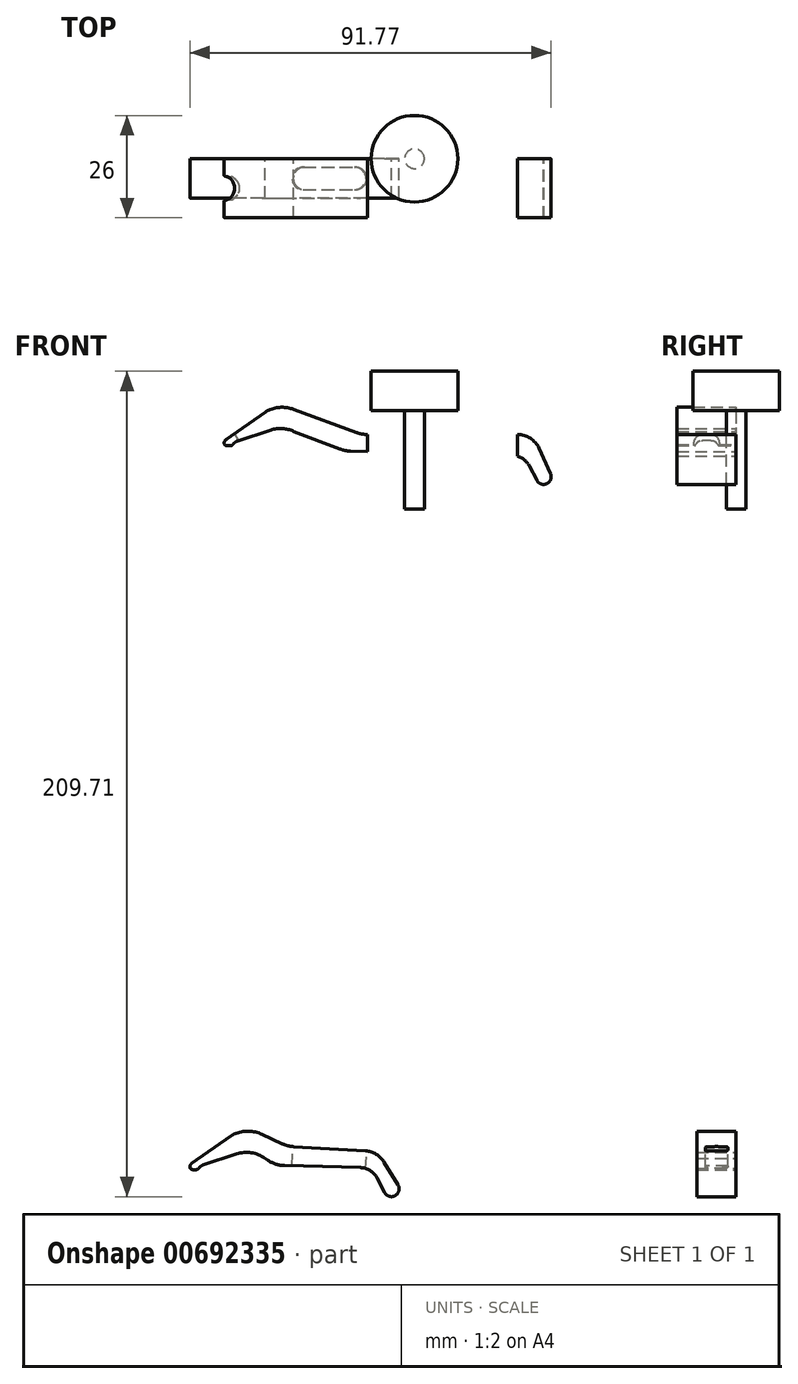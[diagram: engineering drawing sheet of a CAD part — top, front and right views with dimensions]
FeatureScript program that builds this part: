
annotation { "Feature Type Name" : "Feature", "Feature Type Description" : "" }
export const myFeature = defineFeature(function(context is Context, id is Id, definition is map)
    precondition{}
    {
        {
            var Q0;
            Q0=qCreatedBy(makeId("Front.planeOp"),FACE);
            var sketch = newSketch(context, id + "F0", { "sketchPlane" : qUnion([Q0])});
            skLineSegment(sketch, "E0.bottom", {"start": v(-71.92, 0) * mm, "end": v(4.68, 0) * mm});
            skLineSegment(sketch, "E0.top", {"start": v(-71.92, 5) * mm, "end": v(4.68, 5) * mm});
            skLineSegment(sketch, "E0.left", {"start": v(-71.92, 0) * mm, "end": v(-71.92, 5) * mm});
            skLineSegment(sketch, "E0.right", {"start": v(4.68, 0) * mm, "end": v(4.68, 5) * mm});
            skLineSegment(sketch, "E1.bottom", {"start": v(-61.54, 15) * mm, "end": v(0, 15) * mm});
            skLineSegment(sketch, "E1.top", {"start": v(-61.54, 5) * mm, "end": v(0, 5) * mm});
            skLineSegment(sketch, "E1.left", {"start": v(-61.54, 15) * mm, "end": v(-61.54, 5) * mm});
            skLineSegment(sketch, "E1.right", {"start": v(0, 15) * mm, "end": v(0, 5) * mm});
            skLineSegment(sketch, "E2", {"start": v(-10, 41.21) * mm, "end": v(-10, -87.98) * mm, "construction": true});
            skLineSegment(sketch, "E3", {"start": v(69.92, 0) * mm, "end": v(70.03, 0) * mm});
            skLineSegment(sketch, "E4", {"start": v(71.74, 2.83) * mm, "end": v(68.83, 9.2) * mm});
            skLineSegment(sketch, "E5", {"start": v(63.37, 12.7) * mm, "end": v(25.24, 12.7) * mm});
            skPoint(sketch, "E6.visualSharp", {"position": v(50, 0) * mm});
            skPoint(sketch, "E7.visualSharp", {"position": v(73.03, 0) * mm});
            skArc(sketch, "E7.filletArc", {"start": v(69.92, 0) * mm, "mid": v(71.6, 0.92) * mm, "end": v(71.74, 2.83) * mm});
            skLineSegment(sketch, "E8", {"start": v(37.19, 28.77) * mm, "end": v(37.19, -6.23) * mm});
            skLineSegment(sketch, "E9", {"start": v(37.19, -6.23) * mm, "end": v(39.69, -6.23) * mm});
            skLineSegment(sketch, "E10", {"start": v(39.69, -6.23) * mm, "end": v(39.69, 18.77) * mm});
            skLineSegment(sketch, "E11", {"start": v(39.69, 18.77) * mm, "end": v(48.19, 18.77) * mm});
            skLineSegment(sketch, "E12", {"start": v(48.19, 18.77) * mm, "end": v(48.19, 28.77) * mm});
            skLineSegment(sketch, "E13", {"start": v(48.19, 28.77) * mm, "end": v(37.19, 28.77) * mm});
            skLineSegment(sketch, "E14", {"start": v(6.53, 19.1) * mm, "end": v(22.47, 13.2) * mm});
            skArc(sketch, "E15.filletArc", {"start": v(6.53, 19.1) * mm, "mid": v(3.34, 19.62) * mm, "end": v(0.17, 18.91) * mm});
            skPoint(sketch, "E16.visualSharp", {"position": v(23.8, 12.7) * mm});
            skArc(sketch, "E16.filletArc", {"start": v(22.47, 13.2) * mm, "mid": v(23.83, 12.83) * mm, "end": v(25.24, 12.7) * mm});
            skLineSegment(sketch, "E17", {"start": v(68.26, 1.07) * mm, "end": v(66.35, 4.72) * mm});
            skLineSegment(sketch, "E18", {"start": v(-0.7, 18.42) * mm, "end": v(-10.73, 11.4) * mm});
            skLineSegment(sketch, "E19", {"start": v(20.96, 8.48) * mm, "end": v(62.06, 7.4) * mm});
            skLineSegment(sketch, "E20", {"start": v(6.52, 13.5) * mm, "end": v(18.33, 9) * mm});
            skLineSegment(sketch, "E21", {"start": v(0.7, 13.82) * mm, "end": v(-7.82, 11.02) * mm});
            skPoint(sketch, "E22.visualSharp", {"position": v(-0.38, 18.65) * mm});
            skArc(sketch, "E22.filletArc", {"start": v(0.17, 18.91) * mm, "mid": v(-0.27, 18.69) * mm, "end": v(-0.7, 18.42) * mm});
            skArc(sketch, "E23", {"start": v(0.7, 13.82) * mm, "mid": v(3.64, 14.21) * mm, "end": v(6.52, 13.5) * mm});
            skLineSegment(sketch, "E24", {"start": v(-11.16, 10.27) * mm, "end": v(-10.98, 10) * mm});
            skLineSegment(sketch, "E25", {"start": v(-10.35, 9.84) * mm, "end": v(-9.65, 9.84) * mm});
            skLineSegment(sketch, "E26", {"start": v(-8.84, 10.27) * mm, "end": v(-8.83, 10.27) * mm});
            skPoint(sketch, "E27.visualSharp", {"position": v(-10.87, 9.84) * mm});
            skArc(sketch, "E27.filletArc", {"start": v(-11.16, 10.27) * mm, "mid": v(-10.8, 9.95) * mm, "end": v(-10.35, 9.84) * mm});
            skPoint(sketch, "E28.visualSharp", {"position": v(-9.13, 9.84) * mm});
            skArc(sketch, "E28.filletArc", {"start": v(-9.65, 9.84) * mm, "mid": v(-9.2, 9.95) * mm, "end": v(-8.84, 10.27) * mm});
            skPoint(sketch, "E29.visualSharp", {"position": v(-11.55, 10.82) * mm});
            skArc(sketch, "E29.filletArc", {"start": v(-10.73, 11.4) * mm, "mid": v(-11.14, 10.75) * mm, "end": v(-10.98, 10) * mm});
            skPoint(sketch, "E30.visualSharp", {"position": v(-8.45, 10.82) * mm});
            skArc(sketch, "E30.filletArc", {"start": v(-7.82, 11.02) * mm, "mid": v(-8.38, 10.73) * mm, "end": v(-8.83, 10.27) * mm});
            skPoint(sketch, "E31.visualSharp", {"position": v(19.6, 8.52) * mm});
            skArc(sketch, "E31.filletArc", {"start": v(18.33, 9) * mm, "mid": v(19.62, 8.63) * mm, "end": v(20.96, 8.48) * mm});
            skPoint(sketch, "E32.visualSharp", {"position": v(67.23, 12.7) * mm});
            skArc(sketch, "E32.filletArc", {"start": v(68.83, 9.2) * mm, "mid": v(66.61, 11.76) * mm, "end": v(63.37, 12.7) * mm});
            skPoint(sketch, "E33.visualSharp", {"position": v(65, 7.32) * mm});
            skArc(sketch, "E33.filletArc", {"start": v(66.35, 4.72) * mm, "mid": v(64.57, 6.64) * mm, "end": v(62.06, 7.4) * mm});
            skPoint(sketch, "E34.visualSharp", {"position": v(68.82, 0) * mm});
            skArc(sketch, "E34.filletArc", {"start": v(68.26, 1.07) * mm, "mid": v(69, 0.29) * mm, "end": v(70.03, 0) * mm});
            skLineSegment(sketch, "E35", {"start": v(31.28, -180.94) * mm, "end": v(31.4, -180.94) * mm});
            skLineSegment(sketch, "E36", {"start": v(32.99, -177.9) * mm, "end": v(29.5, -172.18) * mm});
            skLineSegment(sketch, "E37", {"start": v(24.73, -169.32) * mm, "end": v(6.47, -168.23) * mm});
            skPoint(sketch, "E38.visualSharp", {"position": v(34.85, -180.94) * mm});
            skArc(sketch, "E38.filletArc", {"start": v(31.28, -180.94) * mm, "mid": v(33.02, -179.92) * mm, "end": v(32.99, -177.9) * mm});
            skLineSegment(sketch, "E39", {"start": v(-1.5, -165.11) * mm, "end": v(3.55, -167.48) * mm});
            skArc(sketch, "E40.filletArc", {"start": v(-1.5, -165.11) * mm, "mid": v(-5, -164.3) * mm, "end": v(-8.52, -165.01) * mm});
            skPoint(sketch, "E41.visualSharp", {"position": v(4.94, -168.14) * mm});
            skArc(sketch, "E41.filletArc", {"start": v(3.55, -167.48) * mm, "mid": v(4.98, -168) * mm, "end": v(6.47, -168.23) * mm});
            skLineSegment(sketch, "E42", {"start": v(29.62, -179.87) * mm, "end": v(27.71, -176.23) * mm});
            skLineSegment(sketch, "E43", {"start": v(-9.4, -165.5) * mm, "end": v(-19.43, -172.53) * mm});
            skLineSegment(sketch, "E44", {"start": v(4.16, -173.04) * mm, "end": v(23.42, -173.55) * mm});
            skLineSegment(sketch, "E45", {"start": v(-0.82, -171.21) * mm, "end": v(0.03, -171.76) * mm});
            skLineSegment(sketch, "E46", {"start": v(-8, -170.1) * mm, "end": v(-16.51, -172.9) * mm});
            skPoint(sketch, "E47.visualSharp", {"position": v(-9.07, -165.28) * mm});
            skArc(sketch, "E47.filletArc", {"start": v(-8.52, -165.01) * mm, "mid": v(-8.97, -165.24) * mm, "end": v(-9.4, -165.5) * mm});
            skArc(sketch, "E48", {"start": v(-8, -170.1) * mm, "mid": v(-4.28, -169.8) * mm, "end": v(-0.82, -171.21) * mm});
            skLineSegment(sketch, "E49", {"start": v(-19.86, -173.66) * mm, "end": v(-19.67, -173.93) * mm});
            skLineSegment(sketch, "E50", {"start": v(-19.04, -174.08) * mm, "end": v(-18.35, -174.08) * mm});
            skLineSegment(sketch, "E51", {"start": v(-17.53, -173.66) * mm, "end": v(-17.53, -173.65) * mm});
            skPoint(sketch, "E52.visualSharp", {"position": v(-19.56, -174.08) * mm});
            skArc(sketch, "E52.filletArc", {"start": v(-19.86, -173.66) * mm, "mid": v(-19.5, -173.97) * mm, "end": v(-19.04, -174.08) * mm});
            skPoint(sketch, "E53.visualSharp", {"position": v(-17.83, -174.08) * mm});
            skArc(sketch, "E53.filletArc", {"start": v(-18.35, -174.08) * mm, "mid": v(-17.89, -173.97) * mm, "end": v(-17.53, -173.66) * mm});
            skPoint(sketch, "E54.visualSharp", {"position": v(-20.25, -173.1) * mm});
            skArc(sketch, "E54.filletArc", {"start": v(-19.43, -172.53) * mm, "mid": v(-19.84, -173.18) * mm, "end": v(-19.67, -173.93) * mm});
            skPoint(sketch, "E55.visualSharp", {"position": v(-17.14, -173.1) * mm});
            skArc(sketch, "E55.filletArc", {"start": v(-16.51, -172.9) * mm, "mid": v(-17.08, -173.2) * mm, "end": v(-17.53, -173.65) * mm});
            skPoint(sketch, "E56.visualSharp", {"position": v(1.91, -172.98) * mm});
            skArc(sketch, "E56.filletArc", {"start": v(0.03, -171.76) * mm, "mid": v(2, -172.68) * mm, "end": v(4.16, -173.04) * mm});
            skPoint(sketch, "E57.visualSharp", {"position": v(27.86, -169.51) * mm});
            skArc(sketch, "E57.filletArc", {"start": v(29.5, -172.18) * mm, "mid": v(27.46, -170.17) * mm, "end": v(24.73, -169.32) * mm});
            skPoint(sketch, "E58.visualSharp", {"position": v(26.35, -173.63) * mm});
            skArc(sketch, "E58.filletArc", {"start": v(27.71, -176.23) * mm, "mid": v(25.93, -174.3) * mm, "end": v(23.42, -173.55) * mm});
            skPoint(sketch, "E59.visualSharp", {"position": v(30.18, -180.94) * mm});
            skArc(sketch, "E59.filletArc", {"start": v(29.62, -179.87) * mm, "mid": v(30.36, -180.65) * mm, "end": v(31.4, -180.94) * mm});
            skSolve(sketch);
        }
        {
            var Q0;
            Q0=makeQuery(id+"F0.imprint","IMPRINT",FACE,{"disambiguationData":[TD([[makeQuery(id+"F0.imprint","IMPRINT",EDGE,{"derivedFrom":sQuery(id+"F0.wireOp",EDGE,"chy2nytO-zmfl-5nmg-iIkC-2bCcduLToJEE")}),1.0]])]});
            var Q1;
            {var subQ0=sQuery(id+"F0.wireOp",EDGE,"E8");var subQ1=sQuery(id+"F0.wireOp",EDGE,"1yFlV4U2-wMyq-fvNE-aanu-wgkpqW72YXBd");var subQ2=makeQuery(id+"F0.imprint","INTERSECT",VERTEX,{"derivedFrom":[subQ1,subQ0]});Q1=makeQuery(id+"F0.imprint","IMPRINT",FACE,{"disambiguationData":[TD([[makeQuery(id+"F0.imprint","IMPRINT",EDGE,{"disambiguationData":[TD([[subQ2,-1.0]])],"derivedFrom":subQ1}),1.0]])]});}
            var Q2;
            Q2=makeQuery(id+"F0.imprint","IMPRINT",FACE,{"disambiguationData":[TD([[makeQuery(id+"F0.imprint","IMPRINT",EDGE,{"derivedFrom":sQuery(id+"F0.wireOp",EDGE,"6blI8IkM-XKw8-aW75-wXaW-XcNFNPNdMWHI")}),1.0]])]});
            var Q3;
            Q3=makeQuery(id+"F0.imprint","IMPRINT",FACE,{"disambiguationData":[TD([[makeQuery(id+"F0.imprint","IMPRINT",EDGE,{"derivedFrom":sQuery(id+"F0.wireOp",EDGE,"E3")}),1.0]])]});
            var Q4;
            Q4=makeQuery(id+"F0.imprint","IMPRINT",FACE,{"disambiguationData":[TD([[makeQuery(id+"F0.imprint","IMPRINT",EDGE,{"derivedFrom":sQuery(id+"F0.wireOp",EDGE,"654yBweP-M0h2-mpYu-GDyn-SHg2XxIWOSnG")}),1.0]])]});
            var Q5;
            Q5=makeQuery(id+"F0.imprint","IMPRINT",FACE,{"disambiguationData":[TD([[makeQuery(id+"F0.imprint","IMPRINT",EDGE,{"derivedFrom":sQuery(id+"F0.wireOp",EDGE,"E14")}),-1.0]])]});
            var Q6;
            {var subQ9=sQuery(id+"F0.wireOp",EDGE,"E4");Q6=makeQuery(id+"F0.imprint","IMPRINT",FACE,{"disambiguationData":[TD([[makeQuery(id+"F0.imprint","IMPRINT",EDGE,{"derivedFrom":subQ9}),1.0]])]});}
            var Q7;
            {var subQ0=sQuery(id+"F0.wireOp",EDGE,"E10");var subQ1=sQuery(id+"F0.wireOp",EDGE,"E5");var subQ2=makeQuery(id+"F0.imprint","INTERSECT",VERTEX,{"derivedFrom":[subQ1,subQ0]});Q7=makeQuery(id+"F0.imprint","IMPRINT",FACE,{"disambiguationData":[TD([[makeQuery(id+"F0.imprint","IMPRINT",EDGE,{"disambiguationData":[TD([[subQ2,-1.0]])],"derivedFrom":subQ1}),1.0]])]});}
            var Q8;
            {var subQ11=sQuery(id+"F0.wireOp",EDGE,"E25");Q8=makeQuery(id+"F0.imprint","IMPRINT",FACE,{"disambiguationData":[TD([[makeQuery(id+"F0.imprint","IMPRINT",EDGE,{"derivedFrom":subQ11}),1.0]])]});}
            extrude(context, id + "F1", {"entities" : qUnion([Q0, Q1, Q2, Q3, Q4, Q5, Q6, Q7, Q8]), "depth" : 15 * mm, "offsetDistance" : 25 * mm});
        }
        {
            var Q0;
            Q0=makeQuery(id+"F1.opExtrude","SWEPT_FACE",FACE,{"disambiguationData":[OSD([sQuery(id+"F0.wireOp",EDGE,"E5")])]});
            var sketch = newSketch(context, id + "F2", { "sketchPlane" : qUnion([Q0])});
            skLineSegment(sketch, "E60", {"start": v(63.37, -7.5) * mm, "end": v(101.37, -7.5) * mm, "construction": true});
            skLineSegment(sketch, "E61", {"start": v(44.3, 13.18) * mm, "end": v(44.3, -39.23) * mm, "construction": true});
            skPoint(sketch, "E61.startSnap0", {"position": v(44.3, 0) * mm});
            skLineSegment(sketch, "E62", {"start": v(28.36, -4.7) * mm, "end": v(60.25, -4.7) * mm});
            skLineSegment(sketch, "E63", {"start": v(60.25, -10.3) * mm, "end": v(28.36, -10.3) * mm});
            skArc(sketch, "E64", {"start": v(60.25, -4.7) * mm, "mid": v(63.05, -7.5) * mm, "end": v(60.25, -10.3) * mm});
            skArc(sketch, "E65", {"start": v(28.36, -4.7) * mm, "mid": v(25.56, -7.5) * mm, "end": v(28.36, -10.3) * mm});
            skSolve(sketch);
        }
        {
            var Q0;
            {var subQ9=sQuery(id+"F2.wireOp",EDGE,"E62");Q0=makeQuery(id+"F2.imprint","IMPRINT",FACE,{"disambiguationData":[TD([[makeQuery(id+"F2.imprint","IMPRINT",EDGE,{"derivedFrom":subQ9}),-1.0]])]});}
            var Q1;
            {var subQ0=sQuery(id+"F2.wireOp",EDGE,"E64");var subQ1=makeQuery(id+"F1.opExtrude","SWEPT_EDGE",EDGE,{"disambiguationData":[OSD([sQuery(id+"F0.wireOp",EDGE,"E5"),sQuery(id+"F0.wireOp",EDGE,"419d96cd-9842-4b0f-b00d-9db5839c5dab.filletArc")])]});var subQ2=makeQuery(id+"F2.imprint","INTERSECT",VERTEX,{"disambiguationData":[OD(0.0)],"derivedFrom":[subQ1,subQ0]});Q1=makeQuery(id+"F2.imprint","IMPRINT",FACE,{"disambiguationData":[TD([[makeQuery(id+"F2.imprint","IMPRINT",EDGE,{"disambiguationData":[TD([[subQ2,-1.0]])],"derivedFrom":subQ0}),-1.0]])]});}
            var Q2;
            {var subQ0=sQuery(id+"F2.wireOp",EDGE,"E65");var subQ1=makeQuery(id+"F1.opExtrude","SWEPT_EDGE",EDGE,{"disambiguationData":[OSD([sQuery(id+"F0.wireOp",EDGE,"E5"),sQuery(id+"F0.wireOp",EDGE,"E16.filletArc")])]});var subQ2=makeQuery(id+"F2.imprint","INTERSECT",VERTEX,{"disambiguationData":[OD(0.0)],"derivedFrom":[subQ1,subQ0]});Q2=makeQuery(id+"F2.imprint","IMPRINT",FACE,{"disambiguationData":[TD([[makeQuery(id+"F2.imprint","IMPRINT",EDGE,{"disambiguationData":[TD([[subQ2,-1.0]])],"derivedFrom":subQ0}),1.0]])]});}
            extrude(context, id + "F3", {"entities" : qUnion([Q0, Q1, Q2]), "operationType" : NewBodyOperationType.REMOVE, "endBound" : BoundingType.THROUGH_ALL, "oppositeDirection" : true, "depth" : 25 * mm, "offsetDistance" : 25 * mm, "hasSecondDirection" : true, "secondDirectionBound" : SecondDirectionBoundingType.THROUGH_ALL, "secondDirectionOppositeDirection" : false, "secondDirectionDepth" : 25 * mm});
        }
        {
            var Q0;
            Q0=makeQuery(id+"F0.imprint","IMPRINT",FACE,{"disambiguationData":[TD([[makeQuery(id+"F0.imprint","IMPRINT",EDGE,{"derivedFrom":sQuery(id+"F0.wireOp",EDGE,"E8")}),1.0]])]});
            var Q1;
            {var subQ0=sQuery(id+"F0.wireOp",EDGE,"E11");Q1=makeQuery(id+"F0.imprint","IMPRINT",FACE,{"disambiguationData":[TD([[makeQuery(id+"F0.imprint","IMPRINT",EDGE,{"derivedFrom":subQ0}),1.0]])]});}
            var Q2;
            Q2=sQuery(id+"F0.wireOp",EDGE,"E8");
            revolve(context, id + "F4", {"entities" : qUnion([Q0, Q1]), "axis" : qUnion([Q2]), "revolveType" : RevolveType.FULL});
        }
        {
            var Q0;
            Q0=makeQuery(id+"F1.opExtrude","SWEPT_FACE",FACE,{"disambiguationData":[OSD([sQuery(id+"F0.wireOp",EDGE,"E18")])]});
            var sketch = newSketch(context, id + "F5", { "sketchPlane" : qUnion([Q0])});
            skLineSegment(sketch, "E66", {"start": v(-7.1, -7.5) * mm, "end": v(13.22, -7.5) * mm, "construction": true});
            skPoint(sketch, "E66.startSnap0", {"position": v(-2.25, -7.5) * mm});
            skLineSegment(sketch, "E67", {"start": v(3.87, -18.28) * mm, "end": v(3.87, 5.07) * mm, "construction": true});
            skPoint(sketch, "E67.startSnap0", {"position": v(3.87, -15) * mm});
            skLineSegment(sketch, "E68", {"start": v(-1.89, -10.42) * mm, "end": v(-5.57, -11.28) * mm});
            skLineSegment(sketch, "E69", {"start": v(-5.57, -11.28) * mm, "end": v(-5.57, -3.72) * mm});
            skLineSegment(sketch, "E70", {"start": v(-5.57, -3.72) * mm, "end": v(-1.89, -4.58) * mm});
            skLineSegment(sketch, "E71", {"start": v(0.43, -7.5) * mm, "end": v(0.43, -7.5) * mm});
            skPoint(sketch, "E72.visualSharp", {"position": v(0.43, -9.88) * mm});
            skArc(sketch, "E72.filletArc", {"start": v(-1.89, -10.42) * mm, "mid": v(-0.22, -9.36) * mm, "end": v(0.43, -7.5) * mm});
            skPoint(sketch, "E73.visualSharp", {"position": v(0.43, -5.12) * mm});
            skArc(sketch, "E73.filletArc", {"start": v(0.43, -7.5) * mm, "mid": v(-0.22, -5.64) * mm, "end": v(-1.89, -4.58) * mm});
            skLineSegment(sketch, "E74", {"start": v(-2.25, -10.48) * mm, "end": v(-2.25, -4.52) * mm});
            skSolve(sketch);
        }
        {
            var Q0;
            {var subQ0=sQuery(id+"F5.wireOp",EDGE,"E71");Q0=makeQuery(id+"F5.imprint","IMPRINT",FACE,{"disambiguationData":[TD([[makeQuery(id+"F5.imprint","IMPRINT",EDGE,{"derivedFrom":subQ0}),-1.0]])]});}
            var Q1;
            {var subQ1=sQuery(id+"F5.wireOp",EDGE,"E68");Q1=makeQuery(id+"F5.imprint","IMPRINT",FACE,{"disambiguationData":[TD([[makeQuery(id+"F5.imprint","IMPRINT",EDGE,{"derivedFrom":subQ1}),-1.0]])]});}
            var Q2;
            {var subQ4=sQuery(id+"F5.wireOp",EDGE,"E72.filletArc");Q2=makeQuery(id+"F5.imprint","IMPRINT",FACE,{"disambiguationData":[TD([[makeQuery(id+"F5.imprint","IMPRINT",EDGE,{"derivedFrom":subQ4}),1.0]])]});}
            extrude(context, id + "F6", {"entities" : qUnion([Q0, Q1, Q2]), "operationType" : NewBodyOperationType.REMOVE, "endBound" : BoundingType.THROUGH_ALL, "oppositeDirection" : true, "depth" : 12 * mm, "offsetDistance" : 25 * mm});
        }
        {
            var Q0;
            {var subQ6=sQuery(id+"F0.wireOp",EDGE,"E36");Q0=makeQuery(id+"F0.imprint","IMPRINT",FACE,{"disambiguationData":[TD([[makeQuery(id+"F0.imprint","IMPRINT",EDGE,{"derivedFrom":subQ6}),1.0]])]});}
            extrude(context, id + "F7", {"entities" : qUnion([Q0]), "depth" : 10 * mm, "offsetDistance" : 25 * mm});
        }
        {
            var Q0;
            Q0=makeQuery(id+"F7.opExtrude","SWEPT_FACE",FACE,{"disambiguationData":[OSD([sQuery(id+"F0.wireOp",EDGE,"E37")])]});
            var sketch = newSketch(context, id + "F8", { "sketchPlane" : qUnion([Q0])});
            skLineSegment(sketch, "E75", {"start": v(48.81, -5) * mm, "end": v(-37.71, -5) * mm, "construction": true});
            skPoint(sketch, "E75.startSnap0", {"position": v(16.53, -5) * mm});
            skPoint(sketch, "E75.endSnap0", {"position": v(16.53, -5) * mm});
            skLineSegment(sketch, "E76.bottom", {"start": v(19.28, -2.15) * mm, "end": v(32.28, -2.15) * mm});
            skLineSegment(sketch, "E76.top", {"start": v(19.28, -7.85) * mm, "end": v(32.28, -7.85) * mm});
            skArc(sketch, "E77", {"start": v(19.28, -2.15) * mm, "mid": v(16.43, -5) * mm, "end": v(19.28, -7.85) * mm});
            skArc(sketch, "E78", {"start": v(32.28, -2.15) * mm, "mid": v(35.13, -5) * mm, "end": v(32.28, -7.85) * mm});
            skLineSegment(sketch, "E79", {"start": v(25.78, 1.78) * mm, "end": v(25.78, -18.04) * mm, "construction": true});
            skPoint(sketch, "E79.startSnap0", {"position": v(25.78, -2.15) * mm});
            skSolve(sketch);
        }
        {
            var Q0;
            Q0 = qSketchRegion(id + "F8", true);
            extrude(context, id + "F9", {"entities" : qUnion([Q0]), "operationType" : NewBodyOperationType.REMOVE, "endBound" : BoundingType.THROUGH_ALL, "oppositeDirection" : true, "depth" : 25 * mm, "offsetDistance" : 25 * mm});
        }
    });
